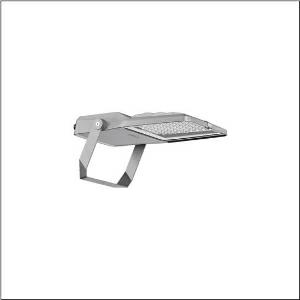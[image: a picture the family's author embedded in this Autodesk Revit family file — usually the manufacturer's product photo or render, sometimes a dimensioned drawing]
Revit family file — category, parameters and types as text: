
# Revit family: floodlight_fl_21_mini___pl52_5xa7776d4d1a_fa17
name_source: partatom
category: Lighting Fixtures
units: mm (PartAtom-declared; Revit-internal decimal feet)

## family parameters
Cut with Voids When Loaded = No
Host = Face
Light Source = No
Part Type = Normal
Room Calculation Point = No
Round Connector Dimension = Use Diameter
Shared = No

## types (1)
- --- (1 x LED, 18600 lm, 142.9 W, 4000K)
    Apparent Load = 143 VA
    CIE Flux Codes = 26 60 98 100 100
    Color Rendering = 70
    Color Temperature = 4000K
    Default Elevation = 1800 mm
    Description = Floodlight FL 21 mini, floodlight, primary light control with lens, of PMMA, primary optical cover: protective disc, of toughened safety glass, transparent, light distribution: PL52, light emission: direct distribution, installation type: surface-mounted, LED, High Power LED, rated luminous flux: 18.600lm, luminous efficacy: 130lm/W, light colour: 740, colour temperature: 4000K, control gear: D4iSmart Interface (Zhaga), control: overheat protection, constant luminous flux control, time-dependent luminous flux control, flexible luminous flux parameterisation, pre-setting: logarithmic dimming characteristic, with terminal, 6-pole, mains connection: 220..240V, AC, 50/60Hz, start of lifetime: 143W, end of service life: 151W, reduction: 63W, mounting bracket, of diecast aluminium, powder-coated, SITECO metallic grey (DB 702S), corrosivity category C5 mid according to DIN EN ISO 12944, suitable for swimming pools, chlorine-resistant, sealing non-destructively replaceable, mounting bracket, of steel, galvanised, powder-coated, SITECO metallic grey (DB 702S), Smart Interface below and above, protection rating (complete): IP66, insulation class (complete): insulation class II (safety insulation), certification: CE, ENEC, VDE, protection symbol: D, impact resistance: IK08, permissible operating ambient temperature: -40..+40°C, permissible operating ambient temperature for outdoor applications: -40..+50°C, standard: DIN EN 12944, LABS conformity tested according to VDMA 24364:2018-05, packaging unit: 1 piece

Light Distribution: PL52
    Height = 70 mm
    Lamp = 1 x LED
    Lamp Light Flux = 18600 lm
    Lamp Power = 142.9 W
    Lamp count = 1
    Length = 485 mm
    Luminous efficacy = 130 lm/W
    Manufacturer = Siteco
    ModVariant = No
    Model = 5XA7776D4D1A
    Number of Poles = 1
    OnlyDefault = Yes
    Power Factor = 1
    Product Name = Floodlight FL 21 mini | PL52
    Product group = floodlight | pylon annexe
    ProductGroupID = 6201
    Protection Class = Protection class II
    Protection Degree = IP 66
    RLX_Detail_Level = 1
    RLX_Emergency_Light_Flux = 0 lm
    RLX_Emergency_Type = 0
    RLX_Emergency_Type_DB = No
    RlxData = <blob elided: 96509 chars, md5=ea8c6ae4>
    Socket = socket
    Standby Power = 0 W
    System Light Flux = 18600 lm
    System Power = 143 W
    Type Comments = factory setting: luminous flux: 100 % | dim-lin: 254 | 730 mA
    Type Image = l_1006845.jpg
    URL = http://relux.com
    VarID = @adj_099301
    Voltage = 0 V
    Weight = 0.00 kg
    Width = 337 mm

## geometry (parser evidence)
native form markers: Blend x4, Sweep x11
no freeform markers — native parametric forms only
